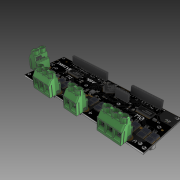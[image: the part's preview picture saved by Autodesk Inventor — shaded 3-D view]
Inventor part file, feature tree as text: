
AUTODESK INVENTOR PART (.ipt)
format: ipt  version: 2018.2 (Build 222227000, 227)  size: 21,693,952 bytes
history: native  units: mm
features: other x279, sketch x3
ambient origin geometry x8: Origin, YZ Plane, XZ Plane, XY Plane, X Axis, Y Axis, Z Axis, Center Point
bodies: Solid1 (feature_tree)
feature tree (282):
  other  "PCBasembly.iam"
  other  "Board.ipt:1"
  other  "R58.iam:1::RES_0603_(1608_metric).ipt:1"
  other  "LED1.iam:1::LED_0603_APT1608_GREEN.ipt:1"
  other  "TP3.iam:1::886587760.iam:1::Cylinder.ipt:1"
  other  "TP2.iam:1::886587760.iam:1::Cylinder.ipt:1"
  other  "TP1.iam:1::886587632.iam:1::Cylinder_1.ipt:1"
  other  "C48.iam:1::899959440.iam:1::Extruded.ipt:1"
  other  "C48.iam:1::899959304.iam:1::Extruded_1.ipt:1"
  other  "C48.iam:1::899959304.iam:2::Extruded_1.ipt:1"
  other  "R34.iam:1::RES_0603_(1608_metric).ipt:1"
  other  "R33.iam:1::RES_0603_(1608_metric).ipt:1"
  other  "R32.iam:1::RES_0603_(1608_metric).ipt:1"
  other  "R48.iam:1::RES_0603_(1608_metric).ipt:1"
  other  "R46.iam:1::899960256.iam:1::Extruded_3.ipt:1"
  other  "R46.iam:1::899960392.iam:1::Extruded_4.ipt:1"
  other  "R46.iam:1::899960256.iam:2::Extruded_3.ipt:1"
  other  "R45.iam:1::899960256.iam:1::Extruded_3.ipt:1"
  other  "R45.iam:1::899960392.iam:1::Extruded_4.ipt:1"
  other  "R45.iam:1::899960256.iam:2::Extruded_3.ipt:1"
  other  "R43.iam:1::RES_0603_(1608_metric).ipt:1"
  other  "R42.iam:1::RES_0603_(1608_metric).ipt:1"
  other  "R41.iam:1::RES_0603_(1608_metric).ipt:1"
  other  "R40.iam:1::RES_0603_(1608_metric).ipt:1"
  other  "R39.iam:1::RES_0603_(1608_metric).ipt:1"
  other  "R38.iam:1::RES_0603_(1608_metric).ipt:1"
  other  "R37.iam:1::RES_0603_(1608_metric).ipt:1"
  other  "R36.iam:1::RES_0603_(1608_metric).ipt:1"
  other  "R35.iam:1::RES_0603_(1608_metric).ipt:1"
  other  "C57.iam:1::899958488.iam:1::Extruded_5.ipt:1"
  other  "C57.iam:1::899958352.iam:1::Extruded_6.ipt:1"
  other  "C57.iam:1::899958352.iam:2::Extruded_6.ipt:1"
  other  "C56.iam:1::899958488.iam:1::Extruded_5.ipt:1"
  other  "C56.iam:1::899958352.iam:1::Extruded_6.ipt:1"
  other  "C56.iam:1::899958352.iam:2::Extruded_6.ipt:1"
  other  "C44.iam:1::899959032.iam:1::Extruded_7.ipt:1"
  other  "C44.iam:1::899959168.iam:1::Extruded_8.ipt:1"
  other  "C44.iam:1::899959032.iam:2::Extruded_7.ipt:1"
  other  "C52.iam:1::899959440.iam:1::Extruded.ipt:1"
  other  "C52.iam:1::899959304.iam:1::Extruded_1.ipt:1"
  other  "C52.iam:1::899959304.iam:2::Extruded_1.ipt:1"
  other  "C51.iam:1::899959440.iam:1::Extruded.ipt:1"
  other  "C51.iam:1::899959304.iam:1::Extruded_1.ipt:1"
  other  "C51.iam:1::899959304.iam:2::Extruded_1.ipt:1"
  other  "C50.iam:1::899959440.iam:1::Extruded.ipt:1"
  other  "C50.iam:1::899959304.iam:1::Extruded_1.ipt:1"
  other  "C50.iam:1::899959304.iam:2::Extruded_1.ipt:1"
  other  "C49.iam:1::899959440.iam:1::Extruded.ipt:1"
  other  "C49.iam:1::899959304.iam:1::Extruded_1.ipt:1"
  other  "C49.iam:1::899959304.iam:2::Extruded_1.ipt:1"
  other  "C47.iam:1::899959440.iam:1::Extruded.ipt:1"
  other  "C47.iam:1::899959304.iam:1::Extruded_1.ipt:1"
  other  "C47.iam:1::899959304.iam:2::Extruded_1.ipt:1"
  other  "C46.iam:1::899959440.iam:1::Extruded.ipt:1"
  other  "C46.iam:1::899959304.iam:1::Extruded_1.ipt:1"
  other  "C46.iam:1::899959304.iam:2::Extruded_1.ipt:1"
  other  "C45.iam:1::899959440.iam:1::Extruded.ipt:1"
  other  "C45.iam:1::899959304.iam:1::Extruded_1.ipt:1"
  other  "C45.iam:1::899959304.iam:2::Extruded_1.ipt:1"
  other  "C55.iam:1::899959032.iam:1::Extruded_7.ipt:1"
  other  "C55.iam:1::899959168.iam:1::Extruded_8.ipt:1"
  other  "C55.iam:1::899959032.iam:2::Extruded_7.ipt:1"
  other  "C18.iam:1::CAP_Alum_Elec_Size_G.ipt:1"
  other  "C17.iam:1::CAP_Alum_Elec_Size_G.ipt:1"
  other  "C16.iam:1::CAP_Alum_Elec_Size_G.ipt:1"
  other  "C43.iam:1::899958488.iam:1::Extruded_5.ipt:1"
  other  "C43.iam:1::899958352.iam:1::Extruded_6.ipt:1"
  other  "C43.iam:1::899958352.iam:2::Extruded_6.ipt:1"
  other  "C1.iam:1::899958488.iam:1::Extruded_5.ipt:1"
  other  "C1.iam:1::899958352.iam:1::Extruded_6.ipt:1"
  other  "C1.iam:1::899958352.iam:2::Extruded_6.ipt:1"
  other  "C2.iam:1::899958488.iam:1::Extruded_5.ipt:1"
  other  "C2.iam:1::899958352.iam:1::Extruded_6.ipt:1"
  other  "C2.iam:1::899958352.iam:2::Extruded_6.ipt:1"
  other  "C3.iam:1::899958488.iam:1::Extruded_5.ipt:1"
  other  "C3.iam:1::899958352.iam:1::Extruded_6.ipt:1"
  other  "C3.iam:1::899958352.iam:2::Extruded_6.ipt:1"
  other  "C4.iam:1::899958488.iam:1::Extruded_5.ipt:1"
  other  "C4.iam:1::899958352.iam:1::Extruded_6.ipt:1"
  other  "C4.iam:1::899958352.iam:2::Extruded_6.ipt:1"
  other  "C5.iam:1::899958488.iam:1::Extruded_5.ipt:1"
  other  "C5.iam:1::899958352.iam:1::Extruded_6.ipt:1"
  other  "C5.iam:1::899958352.iam:2::Extruded_6.ipt:1"
  other  "C6.iam:1::899958488.iam:1::Extruded_5.ipt:1"
  other  "C6.iam:1::899958352.iam:1::Extruded_6.ipt:1"
  other  "C6.iam:1::899958352.iam:2::Extruded_6.ipt:1"
  other  "C7.iam:1::899958488.iam:1::Extruded_5.ipt:1"
  other  "C7.iam:1::899958352.iam:1::Extruded_6.ipt:1"
  other  "C7.iam:1::899958352.iam:2::Extruded_6.ipt:1"
  other  "C8.iam:1::899958488.iam:1::Extruded_5.ipt:1"
  other  "C8.iam:1::899958352.iam:1::Extruded_6.ipt:1"
  other  "C8.iam:1::899958352.iam:2::Extruded_6.ipt:1"
  other  "C9.iam:1::899958488.iam:1::Extruded_5.ipt:1"
  other  "C9.iam:1::899958352.iam:1::Extruded_6.ipt:1"
  other  "C9.iam:1::899958352.iam:2::Extruded_6.ipt:1"
  other  "C10.iam:1::899958488.iam:1::Extruded_5.ipt:1"
  other  "C10.iam:1::899958352.iam:1::Extruded_6.ipt:1"
  other  "C10.iam:1::899958352.iam:2::Extruded_6.ipt:1"
  other  "C11.iam:1::CAP_Alum_Elec_Size_G.ipt:1"
  other  "C12.iam:1::CAP_Alum_Elec_Size_G.ipt:1"
  other  "C13.iam:1::CAP_Alum_Elec_Size_G.ipt:1"
  other  "C14.iam:1::CAP_Alum_Elec_Size_G.ipt:1"
  other  "C15.iam:1::CAP_Alum_Elec_Size_G.ipt:1"
  other  "C20.iam:1::899959032.iam:1::Extruded_7.ipt:1"
  other  "C20.iam:1::899959032.iam:2::Extruded_7.ipt:1"
  other  "C20.iam:1::899959168.iam:1::Extruded_8.ipt:1"
  other  "C21.iam:1::899959032.iam:1::Extruded_7.ipt:1"
  other  "C21.iam:1::899959032.iam:2::Extruded_7.ipt:1"
  other  "C21.iam:1::899959168.iam:1::Extruded_8.ipt:1"
  other  "C22.iam:1::899959440.iam:1::Extruded.ipt:1"
  other  "C22.iam:1::899959304.iam:1::Extruded_1.ipt:1"
  other  "C22.iam:1::899959304.iam:2::Extruded_1.ipt:1"
  other  "C23.iam:1::899958488.iam:1::Extruded_5.ipt:1"
  other  "C23.iam:1::899958352.iam:1::Extruded_6.ipt:1"
  other  "C23.iam:1::899958352.iam:2::Extruded_6.ipt:1"
  other  "C24.iam:1::899959440.iam:1::Extruded.ipt:1"
  other  "C24.iam:1::899959304.iam:1::Extruded_1.ipt:1"
  other  "C24.iam:1::899959304.iam:2::Extruded_1.ipt:1"
  other  "C25.iam:1::899959440.iam:1::Extruded.ipt:1"
  other  "C25.iam:1::899959304.iam:1::Extruded_1.ipt:1"
  other  "C25.iam:1::899959304.iam:2::Extruded_1.ipt:1"
  other  "C26.iam:1::899959032.iam:1::Extruded_7.ipt:1"
  other  "C26.iam:1::899959168.iam:1::Extruded_8.ipt:1"
  other  "C26.iam:1::899959032.iam:2::Extruded_7.ipt:1"
  other  "C27.iam:1::899959440.iam:1::Extruded.ipt:1"
  other  "C27.iam:1::899959304.iam:1::Extruded_1.ipt:1"
  other  "C27.iam:1::899959304.iam:2::Extruded_1.ipt:1"
  other  "C28.iam:1::899959440.iam:1::Extruded.ipt:1"
  other  "C28.iam:1::899959304.iam:1::Extruded_1.ipt:1"
  other  "C28.iam:1::899959304.iam:2::Extruded_1.ipt:1"
  other  "C29.iam:1::899958760.iam:1::Extruded_9.ipt:1"
  other  "C29.iam:1::899958896.iam:1::Extruded_10.ipt:1"
  other  "C29.iam:1::899958760.iam:2::Extruded_9.ipt:1"
  other  "C30.iam:1::899959440.iam:1::Extruded.ipt:1"
  other  "C30.iam:1::899959304.iam:1::Extruded_1.ipt:1"
  other  "C30.iam:1::899959304.iam:2::Extruded_1.ipt:1"
  other  "C31.iam:1::899959440.iam:1::Extruded.ipt:1"
  other  "C31.iam:1::899959304.iam:1::Extruded_1.ipt:1"
  other  "C31.iam:1::899959304.iam:2::Extruded_1.ipt:1"
  other  "C32.iam:1::899958488.iam:1::Extruded_5.ipt:1"
  other  "C32.iam:1::899958352.iam:1::Extruded_6.ipt:1"
  other  "C32.iam:1::899958352.iam:2::Extruded_6.ipt:1"
  other  "C33.iam:1::899959440.iam:1::Extruded.ipt:1"
  other  "C33.iam:1::899959304.iam:1::Extruded_1.ipt:1"
  other  "C33.iam:1::899959304.iam:2::Extruded_1.ipt:1"
  other  "C34.iam:1::899959440.iam:1::Extruded.ipt:1"
  other  "C34.iam:1::899959304.iam:1::Extruded_1.ipt:1"
  other  "C34.iam:1::899959304.iam:2::Extruded_1.ipt:1"
  other  "C35.iam:1::899959440.iam:1::Extruded.ipt:1"
  other  "C35.iam:1::899959304.iam:1::Extruded_1.ipt:1"
  other  "C35.iam:1::899959304.iam:2::Extruded_1.ipt:1"
  other  "C36.iam:1::899959440.iam:1::Extruded.ipt:1"
  other  "C36.iam:1::899959304.iam:1::Extruded_1.ipt:1"
  other  "C36.iam:1::899959304.iam:2::Extruded_1.ipt:1"
  other  "C37.iam:1::899958488.iam:1::Extruded_5.ipt:1"
  other  "C37.iam:1::899958352.iam:1::Extruded_6.ipt:1"
  other  "C37.iam:1::899958352.iam:2::Extruded_6.ipt:1"
  other  "C40.iam:1::899959032.iam:1::Extruded_7.ipt:1"
  other  "C40.iam:1::899959168.iam:1::Extruded_8.ipt:1"
  other  "C40.iam:1::899959032.iam:2::Extruded_7.ipt:1"
  other  "C41.iam:1::899958488.iam:1::Extruded_5.ipt:1"
  other  "C41.iam:1::899958352.iam:1::Extruded_6.ipt:1"
  other  "C41.iam:1::899958352.iam:2::Extruded_6.ipt:1"
  other  "C42.iam:1::899958488.iam:1::Extruded_5.ipt:1"
  other  "C42.iam:1::899958352.iam:1::Extruded_6.ipt:1"
  other  "C42.iam:1::899958352.iam:2::Extruded_6.ipt:1"
  other  "C58.iam:1::899958488.iam:1::Extruded_5.ipt:1"
  other  "C58.iam:1::899958352.iam:1::Extruded_6.ipt:1"
  other  "C58.iam:1::899958352.iam:2::Extruded_6.ipt:1"
  other  "C59.iam:1::899959440.iam:1::Extruded.ipt:1"
  other  "C59.iam:1::899959304.iam:1::Extruded_1.ipt:1"
  other  "C59.iam:1::899959304.iam:2::Extruded_1.ipt:1"
  other  "C61.iam:1::899958488.iam:1::Extruded_5.ipt:1"
  other  "C61.iam:1::899958352.iam:1::Extruded_6.ipt:1"
  other  "C61.iam:1::899958352.iam:2::Extruded_6.ipt:1"
  other  "C62.iam:1::899959440.iam:1::Extruded.ipt:1"
  other  "C62.iam:1::899959304.iam:1::Extruded_1.ipt:1"
  other  "C62.iam:1::899959304.iam:2::Extruded_1.ipt:1"
  other  "C63.iam:1::899959440.iam:1::Extruded.ipt:1"
  other  "C63.iam:1::899959304.iam:1::Extruded_1.ipt:1"
  other  "C63.iam:1::899959304.iam:2::Extruded_1.ipt:1"
  other  "D1.iam:1::899958624.iam:1::Extruded_11.ipt:1"
  other  "D2.iam:1::899958624.iam:1::Extruded_11.ipt:1"
  other  "L2.iam:1::899960800.iam:1::Extruded_12.ipt:1"
  other  "L2.iam:1::899960936.iam:1::Extruded_13.ipt:1"
  other  "L2.iam:1::899960936.iam:2::Extruded_13.ipt:1"
  other  "R1.iam:1::RES_0603_(1608_metric).ipt:1"
  other  "R3.iam:1::RES_0603_(1608_metric).ipt:1"
  other  "R5.iam:1::RES_0603_(1608_metric).ipt:1"
  other  "R6.iam:1::RES_0603_(1608_metric).ipt:1"
  other  "R7.iam:1::RES_0603_(1608_metric).ipt:1"
  other  "R8.iam:1::RES_0603_(1608_metric).ipt:1"
  other  "R9.iam:1::RES_0603_(1608_metric).ipt:1"
  other  "R10.iam:1::RES_0603_(1608_metric).ipt:1"
  other  "R11.iam:1::RES_0603_(1608_metric).ipt:1"
  other  "R13.iam:1::RES_0603_(1608_metric).ipt:1"
  other  "R14.iam:1::RES_0603_(1608_metric).ipt:1"
  other  "R15.iam:1::RES_0603_(1608_metric).ipt:1"
  other  "R16.iam:1::RES_0603_(1608_metric).ipt:1"
  other  "R17.iam:1::RES_0603_(1608_metric).ipt:1"
  other  "R18.iam:1::RES_0603_(1608_metric).ipt:1"
  other  "R19.iam:1::RES_0603_(1608_metric).ipt:1"
  other  "R20.iam:1::RES_0603_(1608_metric).ipt:1"
  other  "R21.iam:1::RES_0603_(1608_metric).ipt:1"
  other  "R22.iam:1::RES_0603_(1608_metric).ipt:1"
  other  "R23.iam:1::RES_0603_(1608_metric).ipt:1"
  other  "R24.iam:1::RES_0603_(1608_metric).ipt:1"
  other  "R25.iam:1::RES_0603_(1608_metric).ipt:1"
  other  "R27.iam:1::899960256.iam:1::Extruded_3.ipt:1"
  other  "R27.iam:1::899960392.iam:1::Extruded_4.ipt:1"
  other  "R27.iam:1::899960256.iam:2::Extruded_3.ipt:1"
  other  "R28.iam:1::899960256.iam:1::Extruded_3.ipt:1"
  other  "R28.iam:1::899960392.iam:1::Extruded_4.ipt:1"
  other  "R28.iam:1::899960256.iam:2::Extruded_3.ipt:1"
  other  "R30.iam:1::RES_0603_(1608_metric).ipt:1"
  other  "R50.iam:1::RES_0603_(1608_metric).ipt:1"
  other  "R51.iam:1::RES_0603_(1608_metric).ipt:1"
  other  "R54.iam:1::RES_0603_(1608_metric).ipt:1"
  other  "R56.iam:1::899960256.iam:1::Extruded_3.ipt:1"
  other  "R56.iam:1::899960392.iam:1::Extruded_4.ipt:1"
  other  "R56.iam:1::899960256.iam:2::Extruded_3.ipt:1"
  other  "R55.iam:1::RES_0603_(1608_metric).ipt:1"
  other  "U3.iam:1::SOT223-4.ipt:1"
  other  "U6.iam:1::899959984.iam:1::Extruded_14.ipt:1"
  other  "U7.iam:1::899960664.iam:1::Extruded_15.ipt:1"
  other  "XT1.iam:1::899960528.iam:1::Extruded_16.ipt:1"
  other  "U1.iam:1::899960664.iam:1::Extruded_15.ipt:1"
  other  "R2.iam:1::RES_0603_(1608_metric).ipt:1"
  other  "R4.iam:1::RES_0603_(1608_metric).ipt:1"
  other  "C38.iam:1::899959440.iam:1::Extruded.ipt:1"
  other  "C38.iam:1::899959304.iam:1::Extruded_1.ipt:1"
  other  "C38.iam:1::899959304.iam:2::Extruded_1.ipt:1"
  other  "C39.iam:1::899959440.iam:1::Extruded.ipt:1"
  other  "C39.iam:1::899959304.iam:1::Extruded_1.ipt:1"
  other  "C39.iam:1::899959304.iam:2::Extruded_1.ipt:1"
  other  "C53.iam:1::899958488.iam:1::Extruded_5.ipt:1"
  other  "C53.iam:1::899958352.iam:1::Extruded_6.ipt:1"
  other  "C53.iam:1::899958352.iam:2::Extruded_6.ipt:1"
  other  "C54.iam:1::899958488.iam:1::Extruded_5.ipt:1"
  other  "C54.iam:1::899958352.iam:1::Extruded_6.ipt:1"
  other  "C54.iam:1::899958352.iam:2::Extruded_6.ipt:1"
  other  "R26.iam:1::RES_0603_(1608_metric).ipt:1"
  other  "R29.iam:1::RES_0603_(1608_metric).ipt:1"
  other  "R44.iam:1::RES_0603_(1608_metric).ipt:1"
  other  "R47.iam:1::RES_0603_(1608_metric).ipt:1"
  other  "R12.iam:1::RES_0402_(1005_metric).ipt:1"
  other  "R31.iam:1::RES_0402_(1005_metric).ipt:1"
  other  "R49.iam:1::RES_0402_(1005_metric).ipt:1"
  other  "C64.iam:1::899958352.iam:1::Extruded_6.ipt:1"
  other  "C64.iam:1::899958352.iam:2::Extruded_6.ipt:1"
  other  "C64.iam:1::899958488.iam:1::Extruded_5.ipt:1"
  other  "R57.iam:1::899959712.iam:1::Extruded_18.ipt:1"
  other  "R57.iam:1::899959712.iam:2::Extruded_18.ipt:1"
  other  "R57.iam:1::899959848.iam:1::Extruded_19.ipt:1"
  other  "C65.iam:1::899959304.iam:1::Extruded_1.ipt:1"
  other  "C65.iam:1::899959304.iam:2::Extruded_1.ipt:1"
  other  "C65.iam:1::899959440.iam:1::Extruded.ipt:1"
  other  "U8.iam:1::SOT23-5.ipt:1"
  other  "C19.iam:1::899959032.iam:1::Extruded_7.ipt:1"
  other  "C19.iam:1::899959168.iam:1::Extruded_8.ipt:1"
  other  "C19.iam:1::899959032.iam:2::Extruded_7.ipt:1"
  other  "C60.iam:1::899958080.iam:1::Extruded_20.ipt:1"
  other  "C60.iam:1::899958216.iam:1::Extruded_21.ipt:1"
  other  "C60.iam:1::899958216.iam:2::Extruded_21.ipt:1"
  other  "partmicro_usb_connector_Shrinkwrap_1.ipt:1"
  other  "mkds_5-3-7.62.ipt:1"
  other  "mkds_5-3-7.62.ipt:2"
  other  "mkds_5-2-7.62.ipt:1"
  other  "mkds_5-2-7.62.ipt:2"
  other  "2DCA56_6P35X3P61.ipt:1"
  other  "2DCA56_6P35X3P61.ipt:2"
  other  "2LQFP-64.ipt:1"
  other  "5pin.ipt:1"
  other  "_18_pin.ipt:1"
  other  "_12_pin.ipt:1"
  other  "Decal1"
  other  "Decal2"
  sketch  "Sketch 1"  dims[d0=10.0mm]
  sketch  "Sketch2"
  other  "Image1"
  sketch  "Sketch3"
  other  "Image2"
